# Revit family: Acoustic-Shell-Tower-Wenger-DIVA-16_32ft--
name_source: partatom
category: Specialty Equipment
revit_build: Autodesk Revit 2018 (Build: 20190510_1515(x64)
units: mm (PartAtom-declared; Revit-internal decimal feet)

## family parameters
Always vertical = Yes
Cut with Voids When Loaded = No
OmniClass Number = 23.21.25.13.11
OmniClass Title = Acoustical Shells
Part Type = Normal
Room Calculation Point = No
Round Connector Dimension = Use Radius
Shared = No
Work Plane-Based = No

## types (1)
- ERROR_LOAD TYPE CATALOG
    Assembly Code = E1020300
    Center Shell Panel Width = 3' - 10"
    Description = Acoustical Tower
    Door Clearance Radius = 3' - 10 5/16"
    ENGworks URL = http://www.ENGworks.com
    Frame Height = 15' - 8 3/16"
    Manufacturer = Wenger
    Model = ST051216
    Overall Height = 16' - 2"
    Overall Width = 12' - 0"
    Panel Depth Offset = 0' - 0 11/16"
    Panel Vertical Offset = 0' - 2"
    Product Page URL = https://www.wengercorp.com
    Series = DIVA®
    Shell Gap Horizontal Offset = 0' - 1 11/32"
    Shell Material = Wood - Wenger - Laminated Veneer Lumber
    Shell Panel Height = 7' - 11 1/2"
    Tapered Shell = No
    Tower Alignment Reference Offset = 6' - 0 11/16"
    Tower Height = 16' - 0"
    Tower Width = 12' - 0"
    URL = https://www.wengercorp.com
    Version = 1

## geometry (parser evidence)
native form markers: Sweep x10
no freeform markers — native parametric forms only
